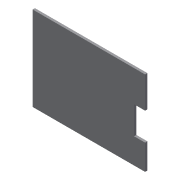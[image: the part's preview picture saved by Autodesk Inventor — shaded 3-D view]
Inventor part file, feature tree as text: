
AUTODESK INVENTOR PART (.ipt)
format: ipt  version: 2016 (Build 200138000, 138)  size: 79,872 bytes
history: native  units: mm
features: extrude x2, sketch x2
ambient origin geometry x8: Origin, YZ Plane, XZ Plane, XY Plane, X Axis, Y Axis, Z Axis, Center Point
bodies: Solid1 (feature_tree)
feature tree (4):
  extrude  "Extrusion1"  Depth=304.8mm
  extrude  "Extrusion2"  Depth=75.0mm
  sketch  "Sketch1"  dims[d0=228.6mm d1=304.8mm]
  sketch  "Sketch2"  dims[d2=6.35mm d3=0.0mm d4=75.0mm d5=85.0mm d6=30.0mm d7=10.0mm d8=0.0mm]
